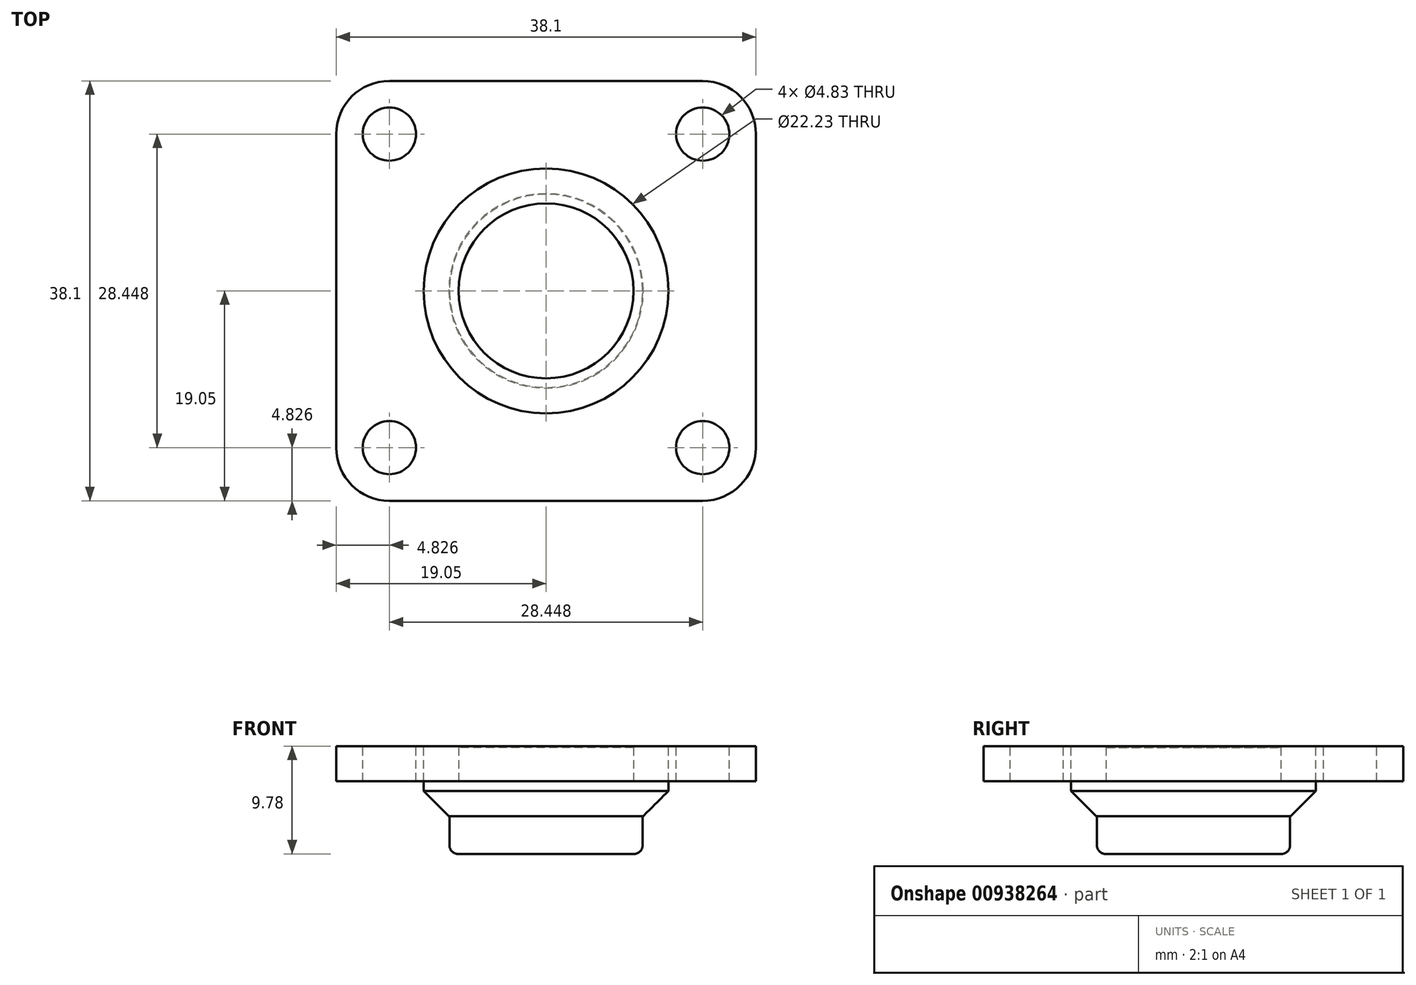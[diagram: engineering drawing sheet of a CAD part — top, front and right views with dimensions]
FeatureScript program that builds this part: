
annotation { "Feature Type Name" : "Feature", "Feature Type Description" : "" }
export const myFeature = defineFeature(function(context is Context, id is Id, definition is map)
    precondition{}
    {
        {
            var Q0;
            Q0=qCreatedBy(makeId("Top.planeOp"),FACE);
            var sketch = newSketch(context, id + "F0", { "sketchPlane" : qUnion([Q0])});
            skLineSegment(sketch, "E0.bottom", {"start": v(19.05, 19.05) * mm, "end": v(-14.22, 19.05) * mm});
            skLineSegment(sketch, "E0.top", {"start": v(19.05, -19.05) * mm, "end": v(-19.05, -19.05) * mm});
            skLineSegment(sketch, "E0.left", {"start": v(19.05, 14.22) * mm, "end": v(19.05, -14.22) * mm});
            skLineSegment(sketch, "E0.right", {"start": v(-19.05, 19.05) * mm, "end": v(-19.05, -14.22) * mm});
            skPoint(sketch, "E0.middle", {"position": v(0, 0) * mm});
            skLineSegment(sketch, "E1", {"start": v(-19.05, 14.22) * mm, "end": v(-19.05, 9.4) * mm});
            skLineSegment(sketch, "E2", {"start": v(14.22, 19.05) * mm, "end": v(9.4, 19.05) * mm});
            skLineSegment(sketch, "E3", {"start": v(-14.22, -19.05) * mm, "end": v(-9.4, -19.05) * mm});
            skLineSegment(sketch, "E4", {"start": v(14.22, -19.05) * mm, "end": v(9.4, -19.05) * mm});
            skPoint(sketch, "E5.visualSharp", {"position": v(-19.05, 19.05) * mm});
            skArc(sketch, "E5.filletArc", {"start": v(-14.22, 19.05) * mm, "mid": v(-17.64, 17.64) * mm, "end": v(-19.05, 14.22) * mm});
            skPoint(sketch, "E6.visualSharp", {"position": v(19.05, 19.05) * mm});
            skArc(sketch, "E6.filletArc", {"start": v(19.05, 14.22) * mm, "mid": v(17.64, 17.64) * mm, "end": v(14.22, 19.05) * mm});
            skPoint(sketch, "E7.visualSharp", {"position": v(19.05, -19.05) * mm});
            skArc(sketch, "E7.filletArc", {"start": v(14.22, -19.05) * mm, "mid": v(17.64, -17.64) * mm, "end": v(19.05, -14.22) * mm});
            skPoint(sketch, "E8.visualSharp", {"position": v(-19.05, -19.05) * mm});
            skArc(sketch, "E8.filletArc", {"start": v(-19.05, -14.22) * mm, "mid": v(-17.64, -17.64) * mm, "end": v(-14.22, -19.05) * mm});
            skPoint(sketch, "E9.visualSharp", {"position": v(-13.34, 15.75) * mm});
            skSolve(sketch);
        }
        {
            var Q0;
            Q0=makeQuery(id+"F0.imprint","IMPRINT",FACE,{"disambiguationData":[TD([[makeQuery(id+"F0.imprint","IMPRINT",EDGE,{"derivedFrom":sQuery(id+"F0.wireOp",EDGE,"E0.left")}),-1.0]])]});
            extrude(context, id + "F1", {"entities" : qUnion([Q0]), "depth" : 3.17 * mm, "offsetDistance" : 25.4 * mm});
        }
        {
            var Q0;
            Q0=makeQuery(id+"F1.opExtrude","CAP_FACE",FACE,{"disambiguationData":[OSD([sQuery(id+"F0.wireOp",EDGE,"E0.bottom"),sQuery(id+"F0.wireOp",EDGE,"E0.top"),sQuery(id+"F0.wireOp",EDGE,"E0.left"),sQuery(id+"F0.wireOp",EDGE,"E0.right"),sQuery(id+"F0.wireOp",EDGE,"E1"),sQuery(id+"F0.wireOp",EDGE,"E2"),sQuery(id+"F0.wireOp",EDGE,"E3"),sQuery(id+"F0.wireOp",EDGE,"E4"),sQuery(id+"F0.wireOp",EDGE,"1NxJJRoS-Ul1q-WfSR-mhbn-pPCNyebDxkPF.bottom"),sQuery(id+"F0.wireOp",EDGE,"1NxJJRoS-Ul1q-WfSR-mhbn-pPCNyebDxkPF.top"),sQuery(id+"F0.wireOp",EDGE,"1NxJJRoS-Ul1q-WfSR-mhbn-pPCNyebDxkPF.left"),sQuery(id+"F0.wireOp",EDGE,"1NxJJRoS-Ul1q-WfSR-mhbn-pPCNyebDxkPF.right"),sQuery(id+"F0.wireOp",EDGE,"DeMJTZG3-CbJ9-Htcv-ZmoL-TmwtIllY4W1o.bottom"),sQuery(id+"F0.wireOp",EDGE,"DeMJTZG3-CbJ9-Htcv-ZmoL-TmwtIllY4W1o.top"),sQuery(id+"F0.wireOp",EDGE,"DeMJTZG3-CbJ9-Htcv-ZmoL-TmwtIllY4W1o.left"),sQuery(id+"F0.wireOp",EDGE,"DeMJTZG3-CbJ9-Htcv-ZmoL-TmwtIllY4W1o.right"),sQuery(id+"F0.wireOp",EDGE,"8dNuNd1F-FUj8-dDWG-4kWf-vYkbyueDwk8T.bottom"),sQuery(id+"F0.wireOp",EDGE,"8dNuNd1F-FUj8-dDWG-4kWf-vYkbyueDwk8T.top"),sQuery(id+"F0.wireOp",EDGE,"8dNuNd1F-FUj8-dDWG-4kWf-vYkbyueDwk8T.left"),sQuery(id+"F0.wireOp",EDGE,"8dNuNd1F-FUj8-dDWG-4kWf-vYkbyueDwk8T.right"),sQuery(id+"F0.wireOp",EDGE,"8p6GbCHx-SLqK-XktK-MZMC-6gaNbOtsdEcP.bottom"),sQuery(id+"F0.wireOp",EDGE,"8p6GbCHx-SLqK-XktK-MZMC-6gaNbOtsdEcP.top"),sQuery(id+"F0.wireOp",EDGE,"8p6GbCHx-SLqK-XktK-MZMC-6gaNbOtsdEcP.left"),sQuery(id+"F0.wireOp",EDGE,"8p6GbCHx-SLqK-XktK-MZMC-6gaNbOtsdEcP.right"),sQuery(id+"F0.wireOp",EDGE,"E5.filletArc"),sQuery(id+"F0.wireOp",EDGE,"E6.filletArc"),sQuery(id+"F0.wireOp",EDGE,"E7.filletArc"),sQuery(id+"F0.wireOp",EDGE,"E8.filletArc"),sQuery(id+"F0.wireOp",EDGE,"E9.filletArc"),sQuery(id+"F0.wireOp",EDGE,"b8d22fb5-f3ba-44bb-a55f-e8a3890e4e18.filletArc"),sQuery(id+"F0.wireOp",EDGE,"9ba0cacd-3eab-4498-b70a-d25d1845bb56.filletArc"),sQuery(id+"F0.wireOp",EDGE,"501b1c14-4091-4061-a1a0-b33761d0eb5d.filletArc"),sQuery(id+"F0.wireOp",EDGE,"76d7186c-e5b1-46d7-a5c3-269453e1b36f.filletArc"),sQuery(id+"F0.wireOp",EDGE,"4994de24-381b-4b70-bc55-e6249ca0c5e7.filletArc"),sQuery(id+"F0.wireOp",EDGE,"03347d0c-9741-420d-99bd-7b8312814912.filletArc"),sQuery(id+"F0.wireOp",EDGE,"35646cd7-ebb3-4241-8fd3-85e50e74c9b5.filletArc"),sQuery(id+"F0.wireOp",EDGE,"3de88156-518b-4375-a48e-84003165f83f.filletArc"),sQuery(id+"F0.wireOp",EDGE,"35acbb21-101a-4c12-8c34-117d548c3c4c.filletArc"),sQuery(id+"F0.wireOp",EDGE,"3ad3c7e6-2c8f-4fbd-8553-b8834501e6ce.filletArc"),sQuery(id+"F0.wireOp",EDGE,"aa7ae870-0608-4778-adc3-97efd9aeb796.filletArc"),sQuery(id+"F0.wireOp",EDGE,"158fd1b0-a534-4424-af99-0c442f11aaa1.filletArc"),sQuery(id+"F0.wireOp",EDGE,"54ee4463-125e-4ea7-8d2f-6b09c4c2a4a1.filletArc"),sQuery(id+"F0.wireOp",EDGE,"b2750d58-4997-47c7-a825-f0c733893089.filletArc"),sQuery(id+"F0.wireOp",EDGE,"c83dade2-9fca-49ad-b666-23e5c8ee6a87.filletArc")])],"isStart":false});
            var sketch = newSketch(context, id + "F2", { "sketchPlane" : qUnion([Q0])});
            skCircle(sketch, "E10", {"center": v(0, 0) * mm, "radius": 22.23 * mm});
            skCircle(sketch, "E11", {"center": v(0, 0) * mm, "radius": 11.11 * mm});
            skSolve(sketch);
        }
        {
            var Q0;
            Q0=makeQuery(id+"F2.imprint","IMPRINT",FACE,{"disambiguationData":[TD([[makeQuery(id+"F2.imprint","IMPRINT",EDGE,{"derivedFrom":sQuery(id+"F2.wireOp",EDGE,"E11")}),1.0]])]});
            var Q1;
            Q1=sQuery(id+"F2.wireOp",EDGE,"E11");
            extrude(context, id + "F3", {"entities" : qUnion([Q0]), "operationType" : NewBodyOperationType.ADD, "surfaceEntities" : qUnion([Q1]), "oppositeDirection" : true, "depth" : 6.35 * mm, "offsetDistance" : 25.4 * mm});
        }
        {
            var Q0;
            Q0=makeQuery(id+"F1.opExtrude","CAP_FACE",FACE,{"disambiguationData":[OSD([sQuery(id+"F0.wireOp",EDGE,"E0.bottom"),sQuery(id+"F0.wireOp",EDGE,"E0.top"),sQuery(id+"F0.wireOp",EDGE,"E0.left"),sQuery(id+"F0.wireOp",EDGE,"E0.right"),sQuery(id+"F0.wireOp",EDGE,"E1"),sQuery(id+"F0.wireOp",EDGE,"E2"),sQuery(id+"F0.wireOp",EDGE,"E3"),sQuery(id+"F0.wireOp",EDGE,"E4"),sQuery(id+"F0.wireOp",EDGE,"1NxJJRoS-Ul1q-WfSR-mhbn-pPCNyebDxkPF.bottom"),sQuery(id+"F0.wireOp",EDGE,"1NxJJRoS-Ul1q-WfSR-mhbn-pPCNyebDxkPF.top"),sQuery(id+"F0.wireOp",EDGE,"1NxJJRoS-Ul1q-WfSR-mhbn-pPCNyebDxkPF.left"),sQuery(id+"F0.wireOp",EDGE,"1NxJJRoS-Ul1q-WfSR-mhbn-pPCNyebDxkPF.right"),sQuery(id+"F0.wireOp",EDGE,"DeMJTZG3-CbJ9-Htcv-ZmoL-TmwtIllY4W1o.bottom"),sQuery(id+"F0.wireOp",EDGE,"DeMJTZG3-CbJ9-Htcv-ZmoL-TmwtIllY4W1o.top"),sQuery(id+"F0.wireOp",EDGE,"DeMJTZG3-CbJ9-Htcv-ZmoL-TmwtIllY4W1o.left"),sQuery(id+"F0.wireOp",EDGE,"DeMJTZG3-CbJ9-Htcv-ZmoL-TmwtIllY4W1o.right"),sQuery(id+"F0.wireOp",EDGE,"8dNuNd1F-FUj8-dDWG-4kWf-vYkbyueDwk8T.bottom"),sQuery(id+"F0.wireOp",EDGE,"8dNuNd1F-FUj8-dDWG-4kWf-vYkbyueDwk8T.top"),sQuery(id+"F0.wireOp",EDGE,"8dNuNd1F-FUj8-dDWG-4kWf-vYkbyueDwk8T.left"),sQuery(id+"F0.wireOp",EDGE,"8dNuNd1F-FUj8-dDWG-4kWf-vYkbyueDwk8T.right"),sQuery(id+"F0.wireOp",EDGE,"8p6GbCHx-SLqK-XktK-MZMC-6gaNbOtsdEcP.bottom"),sQuery(id+"F0.wireOp",EDGE,"8p6GbCHx-SLqK-XktK-MZMC-6gaNbOtsdEcP.top"),sQuery(id+"F0.wireOp",EDGE,"8p6GbCHx-SLqK-XktK-MZMC-6gaNbOtsdEcP.left"),sQuery(id+"F0.wireOp",EDGE,"8p6GbCHx-SLqK-XktK-MZMC-6gaNbOtsdEcP.right"),sQuery(id+"F0.wireOp",EDGE,"E5.filletArc"),sQuery(id+"F0.wireOp",EDGE,"E6.filletArc"),sQuery(id+"F0.wireOp",EDGE,"E7.filletArc"),sQuery(id+"F0.wireOp",EDGE,"E8.filletArc"),sQuery(id+"F0.wireOp",EDGE,"E9.filletArc"),sQuery(id+"F0.wireOp",EDGE,"b8d22fb5-f3ba-44bb-a55f-e8a3890e4e18.filletArc"),sQuery(id+"F0.wireOp",EDGE,"9ba0cacd-3eab-4498-b70a-d25d1845bb56.filletArc"),sQuery(id+"F0.wireOp",EDGE,"501b1c14-4091-4061-a1a0-b33761d0eb5d.filletArc"),sQuery(id+"F0.wireOp",EDGE,"76d7186c-e5b1-46d7-a5c3-269453e1b36f.filletArc"),sQuery(id+"F0.wireOp",EDGE,"4994de24-381b-4b70-bc55-e6249ca0c5e7.filletArc"),sQuery(id+"F0.wireOp",EDGE,"03347d0c-9741-420d-99bd-7b8312814912.filletArc"),sQuery(id+"F0.wireOp",EDGE,"35646cd7-ebb3-4241-8fd3-85e50e74c9b5.filletArc"),sQuery(id+"F0.wireOp",EDGE,"3de88156-518b-4375-a48e-84003165f83f.filletArc"),sQuery(id+"F0.wireOp",EDGE,"35acbb21-101a-4c12-8c34-117d548c3c4c.filletArc"),sQuery(id+"F0.wireOp",EDGE,"3ad3c7e6-2c8f-4fbd-8553-b8834501e6ce.filletArc"),sQuery(id+"F0.wireOp",EDGE,"aa7ae870-0608-4778-adc3-97efd9aeb796.filletArc"),sQuery(id+"F0.wireOp",EDGE,"158fd1b0-a534-4424-af99-0c442f11aaa1.filletArc"),sQuery(id+"F0.wireOp",EDGE,"54ee4463-125e-4ea7-8d2f-6b09c4c2a4a1.filletArc"),sQuery(id+"F0.wireOp",EDGE,"b2750d58-4997-47c7-a825-f0c733893089.filletArc"),sQuery(id+"F0.wireOp",EDGE,"c83dade2-9fca-49ad-b666-23e5c8ee6a87.filletArc")])],"isStart":false});
            var sketch = newSketch(context, id + "F4", { "sketchPlane" : qUnion([Q0])});
            skCircle(sketch, "E12", {"center": v(0, 0) * mm, "radius": 11.11 * mm});
            skSolve(sketch);
        }
        {
            var Q0;
            Q0=makeQuery(id+"F4.imprint","IMPRINT",FACE,{"disambiguationData":[TD([[makeQuery(id+"F4.imprint","IMPRINT",EDGE,{"derivedFrom":sQuery(id+"F4.wireOp",EDGE,"E12")}),1.0]])]});
            extrude(context, id + "F5", {"entities" : qUnion([Q0]), "operationType" : NewBodyOperationType.REMOVE, "oppositeDirection" : true, "depth" : 3.17 * mm, "offsetDistance" : 25.4 * mm});
        }
        {
            var Q0;
            Q0=makeQuery(id+"F1.opExtrude","CAP_FACE",FACE,{"disambiguationData":[OSD([sQuery(id+"F0.wireOp",EDGE,"E0.bottom"),sQuery(id+"F0.wireOp",EDGE,"E0.top"),sQuery(id+"F0.wireOp",EDGE,"E0.left"),sQuery(id+"F0.wireOp",EDGE,"E0.right"),sQuery(id+"F0.wireOp",EDGE,"E1"),sQuery(id+"F0.wireOp",EDGE,"E2"),sQuery(id+"F0.wireOp",EDGE,"E3"),sQuery(id+"F0.wireOp",EDGE,"E4"),sQuery(id+"F0.wireOp",EDGE,"1NxJJRoS-Ul1q-WfSR-mhbn-pPCNyebDxkPF.bottom"),sQuery(id+"F0.wireOp",EDGE,"1NxJJRoS-Ul1q-WfSR-mhbn-pPCNyebDxkPF.top"),sQuery(id+"F0.wireOp",EDGE,"1NxJJRoS-Ul1q-WfSR-mhbn-pPCNyebDxkPF.left"),sQuery(id+"F0.wireOp",EDGE,"1NxJJRoS-Ul1q-WfSR-mhbn-pPCNyebDxkPF.right"),sQuery(id+"F0.wireOp",EDGE,"DeMJTZG3-CbJ9-Htcv-ZmoL-TmwtIllY4W1o.bottom"),sQuery(id+"F0.wireOp",EDGE,"DeMJTZG3-CbJ9-Htcv-ZmoL-TmwtIllY4W1o.top"),sQuery(id+"F0.wireOp",EDGE,"DeMJTZG3-CbJ9-Htcv-ZmoL-TmwtIllY4W1o.left"),sQuery(id+"F0.wireOp",EDGE,"DeMJTZG3-CbJ9-Htcv-ZmoL-TmwtIllY4W1o.right"),sQuery(id+"F0.wireOp",EDGE,"8dNuNd1F-FUj8-dDWG-4kWf-vYkbyueDwk8T.bottom"),sQuery(id+"F0.wireOp",EDGE,"8dNuNd1F-FUj8-dDWG-4kWf-vYkbyueDwk8T.top"),sQuery(id+"F0.wireOp",EDGE,"8dNuNd1F-FUj8-dDWG-4kWf-vYkbyueDwk8T.left"),sQuery(id+"F0.wireOp",EDGE,"8dNuNd1F-FUj8-dDWG-4kWf-vYkbyueDwk8T.right"),sQuery(id+"F0.wireOp",EDGE,"8p6GbCHx-SLqK-XktK-MZMC-6gaNbOtsdEcP.bottom"),sQuery(id+"F0.wireOp",EDGE,"8p6GbCHx-SLqK-XktK-MZMC-6gaNbOtsdEcP.top"),sQuery(id+"F0.wireOp",EDGE,"8p6GbCHx-SLqK-XktK-MZMC-6gaNbOtsdEcP.left"),sQuery(id+"F0.wireOp",EDGE,"8p6GbCHx-SLqK-XktK-MZMC-6gaNbOtsdEcP.right"),sQuery(id+"F0.wireOp",EDGE,"E5.filletArc"),sQuery(id+"F0.wireOp",EDGE,"E6.filletArc"),sQuery(id+"F0.wireOp",EDGE,"E7.filletArc"),sQuery(id+"F0.wireOp",EDGE,"E8.filletArc"),sQuery(id+"F0.wireOp",EDGE,"E9.filletArc"),sQuery(id+"F0.wireOp",EDGE,"b8d22fb5-f3ba-44bb-a55f-e8a3890e4e18.filletArc"),sQuery(id+"F0.wireOp",EDGE,"9ba0cacd-3eab-4498-b70a-d25d1845bb56.filletArc"),sQuery(id+"F0.wireOp",EDGE,"501b1c14-4091-4061-a1a0-b33761d0eb5d.filletArc"),sQuery(id+"F0.wireOp",EDGE,"76d7186c-e5b1-46d7-a5c3-269453e1b36f.filletArc"),sQuery(id+"F0.wireOp",EDGE,"4994de24-381b-4b70-bc55-e6249ca0c5e7.filletArc"),sQuery(id+"F0.wireOp",EDGE,"03347d0c-9741-420d-99bd-7b8312814912.filletArc"),sQuery(id+"F0.wireOp",EDGE,"35646cd7-ebb3-4241-8fd3-85e50e74c9b5.filletArc"),sQuery(id+"F0.wireOp",EDGE,"3de88156-518b-4375-a48e-84003165f83f.filletArc"),sQuery(id+"F0.wireOp",EDGE,"35acbb21-101a-4c12-8c34-117d548c3c4c.filletArc"),sQuery(id+"F0.wireOp",EDGE,"3ad3c7e6-2c8f-4fbd-8553-b8834501e6ce.filletArc"),sQuery(id+"F0.wireOp",EDGE,"aa7ae870-0608-4778-adc3-97efd9aeb796.filletArc"),sQuery(id+"F0.wireOp",EDGE,"158fd1b0-a534-4424-af99-0c442f11aaa1.filletArc"),sQuery(id+"F0.wireOp",EDGE,"54ee4463-125e-4ea7-8d2f-6b09c4c2a4a1.filletArc"),sQuery(id+"F0.wireOp",EDGE,"b2750d58-4997-47c7-a825-f0c733893089.filletArc"),sQuery(id+"F0.wireOp",EDGE,"c83dade2-9fca-49ad-b666-23e5c8ee6a87.filletArc")])],"isStart":true});
            var sketch = newSketch(context, id + "F6", { "sketchPlane" : qUnion([Q0])});
            skCircle(sketch, "E13", {"center": v(0, 0) * mm, "radius": 9.53 * mm});
            skSolve(sketch);
        }
        {
            var Q0;
            Q0=makeQuery(id+"F6.imprint","IMPRINT",FACE,{"disambiguationData":[TD([[makeQuery(id+"F6.imprint","IMPRINT",EDGE,{"derivedFrom":sQuery(id+"F6.wireOp",EDGE,"E13")}),1.0]])]});
            extrude(context, id + "F7", {"entities" : qUnion([Q0]), "depth" : 3.05 * mm, "offsetDistance" : 25.4 * mm});
        }
        {
            var Q0;
            Q0=makeQuery(id+"F5.boolean.opBoolean","COPY",FACE,{"derivedFrom":makeQuery(id+"F5.opExtrude","CAP_FACE",FACE,{"disambiguationData":[OSD([sQuery(id+"F4.wireOp",EDGE,"E12")])],"isStart":false})});
            var sketch = newSketch(context, id + "F8", { "sketchPlane" : qUnion([Q0])});
            skCircle(sketch, "E14", {"center": v(0, 0) * mm, "radius": 7.94 * mm});
            skSolve(sketch);
        }
        {
            var Q0;
            Q0=makeQuery(id+"F8.imprint","IMPRINT",FACE,{"disambiguationData":[TD([[makeQuery(id+"F8.imprint","IMPRINT",EDGE,{"derivedFrom":sQuery(id+"F8.wireOp",EDGE,"E14")}),1.0]])]});
            extrude(context, id + "F9", {"entities" : qUnion([Q0]), "operationType" : NewBodyOperationType.ADD, "depth" : 3.05 * mm, "offsetDistance" : 25.4 * mm});
        }
        {
            var Q0;
            Q0=makeQuery(id+"F3.opExtrude","CAP_FACE",FACE,{"disambiguationData":[OSD([sQuery(id+"F2.wireOp",EDGE,"E11")])],"isStart":false});
            var sketch = newSketch(context, id + "F10", { "sketchPlane" : qUnion([Q0])});
            skCircle(sketch, "E15", {"center": v(0, 0) * mm, "radius": 8.76 * mm});
            skSolve(sketch);
        }
        {
            var Q0;
            Q0=makeQuery(id+"F10.imprint","IMPRINT",FACE,{"disambiguationData":[TD([[makeQuery(id+"F10.imprint","IMPRINT",EDGE,{"derivedFrom":sQuery(id+"F10.wireOp",EDGE,"E15")}),1.0]])]});
            extrude(context, id + "F11", {"entities" : qUnion([Q0]), "operationType" : NewBodyOperationType.ADD, "depth" : 3.43 * mm, "offsetDistance" : 25.4 * mm});
        }
        {
            var Q0;
            Q0=makeQuery(id+"F11.opExtrude","CAP_FACE",FACE,{"disambiguationData":[OSD([sQuery(id+"F10.wireOp",EDGE,"E15")])],"isStart":false});
            fillet(context, id + "F12", {"entities" : qUnion([Q0]), "radius" : 0.76 * mm, "tangentPropagation" : true, "allowEdgeOverflow" : false});
        }
        {
            var Q0;
            Q0=makeQuery(id+"F3.opExtrude","CAP_EDGE",EDGE,{"disambiguationData":[OSD([sQuery(id+"F2.wireOp",EDGE,"E11")])],"isStart":false});
            chamfer(context, id + "F13", {"entities" : qUnion([Q0]), "width" : 2.3 * mm, "tangentPropagation" : true});
        }
        {
            var Q0;
            Q0=sQuery(id+"F0.wireOp",VERTEX,"E7.filletArc.center");
            var Q1;
            Q1=sQuery(id+"F0.wireOp",VERTEX,"E8.filletArc.center");
            var Q2;
            Q2=sQuery(id+"F0.wireOp",VERTEX,"E5.filletArc.center");
            var Q3;
            Q3=sQuery(id+"F0.wireOp",VERTEX,"E6.filletArc.center");
            var Q4;
            Q4=makeQuery(id+"F5.boolean.opBoolean","SPLIT",BODY,{"disambiguationData":[OD(0.0)],"derivedFrom":makeQuery(id+"F1.opExtrude","SWEPT_BODY",BODY,{"disambiguationData":[OSD([sQuery(id+"F0.wireOp",EDGE,"E0.bottom"),sQuery(id+"F0.wireOp",EDGE,"E0.top"),sQuery(id+"F0.wireOp",EDGE,"E0.left"),sQuery(id+"F0.wireOp",EDGE,"E0.right"),sQuery(id+"F0.wireOp",EDGE,"E1"),sQuery(id+"F0.wireOp",EDGE,"E2"),sQuery(id+"F0.wireOp",EDGE,"E3"),sQuery(id+"F0.wireOp",EDGE,"E4"),sQuery(id+"F0.wireOp",EDGE,"E5.filletArc"),sQuery(id+"F0.wireOp",EDGE,"E6.filletArc"),sQuery(id+"F0.wireOp",EDGE,"E7.filletArc"),sQuery(id+"F0.wireOp",EDGE,"E8.filletArc")])]})});
            hole(context, id + "F14", {"style" : HoleStyle.SIMPLE, "endStyle" : HoleEndStyle.THROUGH, "oppositeDirection" : true, "holeDiameter" : 4.83 * mm, "majorDiameter" : 6.35 * mm, "isTappedThrough" : true, "tappedDepth" : 12.7 * mm, "tapClearance" : 3, "locations" : qUnion([Q0, Q1, Q2, Q3]), "scope" : qUnion([Q4]), "startStyle" : HoleStartStyle.SKETCH});
        }
    });
